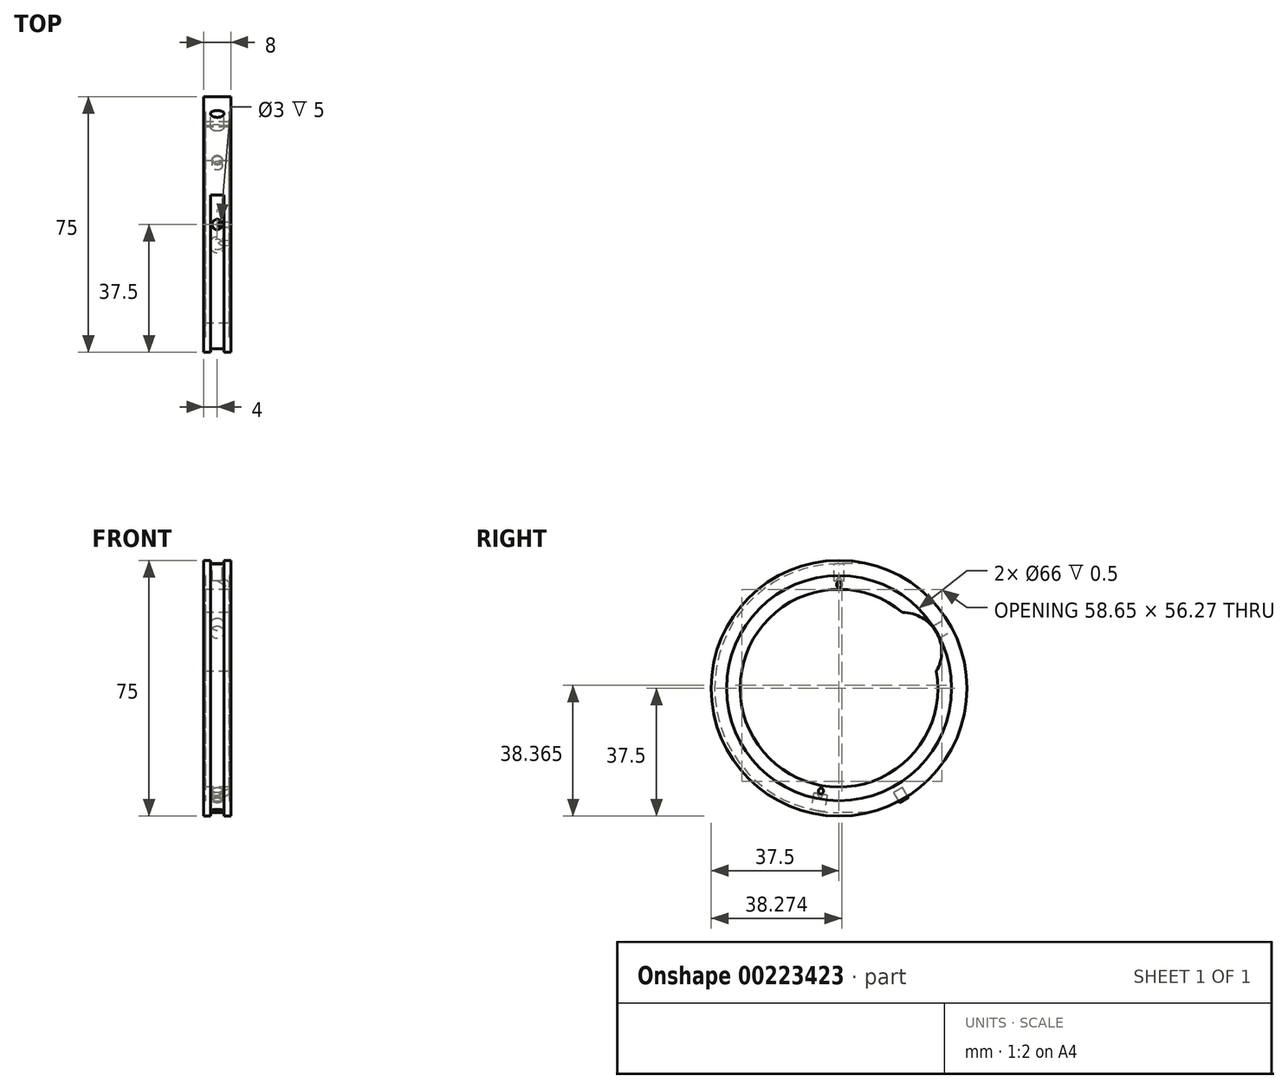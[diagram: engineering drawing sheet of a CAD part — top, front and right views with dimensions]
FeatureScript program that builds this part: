
annotation { "Feature Type Name" : "Feature", "Feature Type Description" : "" }
export const myFeature = defineFeature(function(context is Context, id is Id, definition is map)
    precondition{}
    {
        {
            var Q0;
            Q0=qCreatedBy(makeId("Front.planeOp"),FACE);
            var sketch = newSketch(context, id + "F0", { "sketchPlane" : qUnion([Q0])});
            skLineSegment(sketch, "E0", {"start": v(-4, 37.5) * mm, "end": v(4, 37.5) * mm});
            skLineSegment(sketch, "E1", {"start": v(4, 37.5) * mm, "end": v(4, 33) * mm});
            skLineSegment(sketch, "E2", {"start": v(4, 33) * mm, "end": v(3.5, 33) * mm});
            skLineSegment(sketch, "E3", {"start": v(3.5, 33) * mm, "end": v(3.5, 29) * mm});
            skLineSegment(sketch, "E4", {"start": v(3.5, 29) * mm, "end": v(0, 29) * mm});
            skLineSegment(sketch, "E5.MirrorCS", {"start": v(-4, 33) * mm, "end": v(-3.5, 33) * mm});
            skLineSegment(sketch, "E6.MirrorCS", {"start": v(-3.5, 29) * mm, "end": v(0, 29) * mm});
            skLineSegment(sketch, "E7.MirrorCS", {"start": v(-3.5, 33) * mm, "end": v(-3.5, 29) * mm});
            skLineSegment(sketch, "E8.MirrorCS", {"start": v(-4, 37.5) * mm, "end": v(-4, 33) * mm});
            skLineSegment(sketch, "E9", {"start": v(-6.02, 0) * mm, "end": v(8.87, 0) * mm});
            skSolve(sketch);
        }
        {
            var Q0;
            Q0=makeQuery(id+"F0.imprint","IMPRINT",FACE,{"disambiguationData":[TD([[makeQuery(id+"F0.imprint","IMPRINT",EDGE,{"derivedFrom":sQuery(id+"F0.wireOp",EDGE,"E0")}),-1.0]])]});
            var Q1;
            Q1=sQuery(id+"F0.wireOp",EDGE,"E9");
            revolve(context, id + "F1", {"entities" : qUnion([Q0]), "axis" : qUnion([Q1]), "revolveType" : RevolveType.FULL});
        }
        {
            var Q0;
            Q0=qCreatedBy(makeId("Front.planeOp"),FACE);
            var sketch = newSketch(context, id + "F2", { "sketchPlane" : qUnion([Q0])});
            skLineSegment(sketch, "E10.bottom", {"start": v(-2, 38.5) * mm, "end": v(2, 38.5) * mm});
            skLineSegment(sketch, "E10.top", {"start": v(-2, 36.5) * mm, "end": v(2, 36.5) * mm});
            skLineSegment(sketch, "E10.left", {"start": v(-2, 38.5) * mm, "end": v(-2, 36.5) * mm});
            skLineSegment(sketch, "E10.right", {"start": v(2, 38.5) * mm, "end": v(2, 36.5) * mm});
            skPoint(sketch, "E10.middle", {"position": v(0, 37.5) * mm});
            skLineSegment(sketch, "E11", {"start": v(0, 0) * mm, "end": v(5.52, 0) * mm});
            skPoint(sketch, "E12.orphan", {"position": v(4, 37.5) * mm});
            skPoint(sketch, "E13.orphan", {"position": v(-4, 37.5) * mm});
            skSolve(sketch);
        }
        {
            var Q0;
            {var subQ5=sQuery(id+"F2.wireOp",EDGE,"E10.bottom");Q0=makeQuery(id+"F2.imprint","IMPRINT",FACE,{"disambiguationData":[TD([[makeQuery(id+"F2.imprint","IMPRINT",EDGE,{"derivedFrom":subQ5}),-1.0]])]});}
            var Q1;
            {var subQ5=sQuery(id+"F2.wireOp",EDGE,"E10.top");Q1=makeQuery(id+"F2.imprint","IMPRINT",FACE,{"disambiguationData":[TD([[makeQuery(id+"F2.imprint","IMPRINT",EDGE,{"derivedFrom":subQ5}),1.0]])]});}
            extrude(context, id + "F3", {"entities" : qUnion([Q0, Q1]), "operationType" : NewBodyOperationType.REMOVE, "endBound" : BoundingType.SYMMETRIC, "oppositeDirection" : true, "depth" : 25 * mm});
        }
        {
            var Q0;
            Q0=makeQuery(id+"F3.boolean.opBoolean","COPY",FACE,{"derivedFrom":makeQuery(id+"F3.opExtrude","SWEPT_FACE",FACE,{"disambiguationData":[OSD([sQuery(id+"F2.wireOp",EDGE,"E10.top")])]})});
            var sketch = newSketch(context, id + "F4", { "sketchPlane" : qUnion([Q0])});
            skPoint(sketch, "E14", {"position": v(0, 0) * mm});
            skCircle(sketch, "E15", {"center": v(0, 0) * mm, "radius": 1.5 * mm});
            skSolve(sketch);
        }
        {
            var Q0;
            Q0=makeQuery(id+"F4.imprint","IMPRINT",FACE,{"disambiguationData":[TD([[makeQuery(id+"F4.imprint","IMPRINT",EDGE,{"derivedFrom":sQuery(id+"F4.wireOp",EDGE,"E15")}),1.0]])]});
            extrude(context, id + "F5", {"entities" : qUnion([Q0]), "operationType" : NewBodyOperationType.REMOVE, "oppositeDirection" : true, "depth" : 5 * mm});
        }
        {
            var Q0;
            Q0=makeQuery(id+"F1.opRevolve","SWEPT_FACE",FACE,{"disambiguationData":[OSD([sQuery(id+"F0.wireOp",EDGE,"E7.MirrorCS")])]});
            var sketch = newSketch(context, id + "F6", { "sketchPlane" : qUnion([Q0])});
            skArc(sketch, "E16", {"start": v(-18.66, 22.2) * mm, "mid": v(-28.57, 16.43) * mm, "end": v(-28.57, 4.97) * mm});
            skArc(sketch, "E17.0", {"start": v(-18.66, 22.2) * mm, "mid": v(-25.14, 14.46) * mm, "end": v(-28.57, 4.97) * mm});
            skSolve(sketch);
        }
        {
            var Q0;
            Q0=makeQuery(id+"F6.imprint","IMPRINT",FACE,{"disambiguationData":[TD([[makeQuery(id+"F6.imprint","IMPRINT",EDGE,{"derivedFrom":sQuery(id+"F6.wireOp",EDGE,"E16")}),1.0]])]});
            extrude(context, id + "F7", {"entities" : qUnion([Q0]), "operationType" : NewBodyOperationType.REMOVE, "oppositeDirection" : true, "depth" : 7.5 * mm});
        }
        {
            var Q0;
            Q0=qCreatedBy(makeId("Right.planeOp"),FACE);
            var sketch = newSketch(context, id + "F8", { "sketchPlane" : qUnion([Q0])});
            skLineSegment(sketch, "E18", {"start": v(32.48, 18.75) * mm, "end": v(0, 0) * mm});
            skCircle(sketch, "E19.0", {"center": v(0, 0) * mm, "radius": 37.5 * mm});
            skPoint(sketch, "E20", {"position": v(32.48, 18.75) * mm});
            skSolve(sketch);
        }
        {
            var Q0;
            Q0=sQuery(id+"F8.wireOp",EDGE,"E18");
            var Q1;
            Q1=sQuery(id+"F8.wireOp",VERTEX,"E20");
            cPlane(context, id + "F9", {"entities" : qUnion([Q0, Q1]), "cplaneType" : CPlaneType.CURVE_POINT, "offset" : 25 * mm, "width" : 150 * mm, "height" : 150 * mm});
        }
        {
            var Q0;
            Q0=qCreatedBy(id+"F9.planeOp",FACE);
            var sketch = newSketch(context, id + "F10", { "sketchPlane" : qUnion([Q0])});
            skCircle(sketch, "E21", {"center": v(0, 0) * mm, "radius": 2 * mm});
            skSolve(sketch);
        }
        {
            var Q0;
            Q0=makeQuery(id+"F10.imprint","IMPRINT",FACE,{"disambiguationData":[TD([[makeQuery(id+"F10.imprint","IMPRINT",EDGE,{"derivedFrom":sQuery(id+"F10.wireOp",EDGE,"E21")}),1.0]])]});
            extrude(context, id + "F11", {"entities" : qUnion([Q0]), "operationType" : NewBodyOperationType.REMOVE, "depth" : 25 * mm});
        }
        {
            var Q0;
            Q0=qCreatedBy(makeId("Right.planeOp"),FACE);
            var sketch = newSketch(context, id + "F12", { "sketchPlane" : qUnion([Q0])});
            skLineSegment(sketch, "E22", {"start": v(0, 0) * mm, "end": v(18.75, -32.48) * mm});
            skCircle(sketch, "E23.0", {"center": v(0, 0) * mm, "radius": 37.5 * mm});
            skPoint(sketch, "E24", {"position": v(18.75, -32.48) * mm});
            skLineSegment(sketch, "E25.0", {"start": v(32.48, 18.75) * mm, "end": v(0, 0) * mm});
            skSolve(sketch);
        }
        {
            var Q0;
            Q0=sQuery(id+"F12.wireOp",EDGE,"E22");
            var Q1;
            Q1=sQuery(id+"F12.wireOp",VERTEX,"E24");
            cPlane(context, id + "F13", {"entities" : qUnion([Q0, Q1]), "cplaneType" : CPlaneType.CURVE_POINT, "offset" : 25 * mm, "width" : 150 * mm, "height" : 150 * mm});
        }
        {
            var Q0;
            Q0=qCreatedBy(id+"F13.planeOp",FACE);
            var sketch = newSketch(context, id + "F14", { "sketchPlane" : qUnion([Q0])});
            skCircle(sketch, "E26", {"center": v(0, 0) * mm, "radius": 1.5 * mm});
            skSolve(sketch);
        }
        {
            var Q0;
            Q0=makeQuery(id+"F14.imprint","IMPRINT",FACE,{"disambiguationData":[TD([[makeQuery(id+"F14.imprint","IMPRINT",EDGE,{"derivedFrom":sQuery(id+"F14.wireOp",EDGE,"E26")}),1.0]])]});
            extrude(context, id + "F15", {"entities" : qUnion([Q0]), "operationType" : NewBodyOperationType.REMOVE, "oppositeDirection" : true, "depth" : 3 * mm});
        }
        {
            var Q0;
            Q0=qCreatedBy(makeId("Front.planeOp"),FACE);
            var sketch = newSketch(context, id + "F16", { "sketchPlane" : qUnion([Q0])});
            skLineSegment(sketch, "E27", {"start": v(-4, 37.5) * mm, "end": v(4, 37.5) * mm});
            skLineSegment(sketch, "E28", {"start": v(4, -37.5) * mm, "end": v(-4, -37.5) * mm});
            skLineSegment(sketch, "E29.0", {"start": v(4, 30.06) * mm, "end": v(4, 37.5) * mm, "construction": true});
            skLineSegment(sketch, "E30", {"start": v(1.5, 31.5) * mm, "end": v(4, 30.06) * mm});
            skPoint(sketch, "E31.orphan", {"position": v(4, -37.5) * mm});
            skPoint(sketch, "E32.0.start.orphan", {"position": v(-1.5, 31.5) * mm});
            skPoint(sketch, "E33", {"position": v(4, 30.06) * mm});
            skSolve(sketch);
        }
        {
            var Q0;
            Q0=sQuery(id+"F16.wireOp",EDGE,"E30");
            var Q1;
            Q1=sQuery(id+"F16.wireOp",VERTEX,"E33");
            cPlane(context, id + "F17", {"entities" : qUnion([Q0, Q1]), "cplaneType" : CPlaneType.CURVE_POINT, "offset" : 25 * mm, "width" : 150 * mm, "height" : 150 * mm});
        }
        {
            var Q0;
            Q0=qCreatedBy(id+"F17.planeOp",FACE);
            var sketch = newSketch(context, id + "F18", { "sketchPlane" : qUnion([Q0])});
            skPoint(sketch, "E34.0", {"position": v(0, 28.03) * mm});
            skCircle(sketch, "E35", {"center": v(0, 28.03) * mm, "radius": 0.75 * mm});
            skSolve(sketch);
        }
        {
            var Q0;
            Q0=makeQuery(id+"F18.imprint","IMPRINT",FACE,{"disambiguationData":[TD([[makeQuery(id+"F18.imprint","IMPRINT",EDGE,{"derivedFrom":sQuery(id+"F18.wireOp",EDGE,"E35")}),1.0]])]});
            var Q1;
            Q1=sQuery(id+"F16.wireOp",VERTEX,"E32.0.start.orphan");
            extrude(context, id + "F19", {"entities" : qUnion([Q0]), "operationType" : NewBodyOperationType.REMOVE, "endBound" : BoundingType.UP_TO_VERTEX, "oppositeDirection" : true, "endBoundEntityVertex" : qUnion([Q1]), "depth" : 4 * mm});
        }
        {
            var Q0;
            Q0=qCreatedBy(makeId("Right.planeOp"),FACE);
            var sketch = newSketch(context, id + "F20", { "sketchPlane" : qUnion([Q0])});
            skLineSegment(sketch, "E36", {"start": v(0, 0) * mm, "end": v(-6.51, -36.93) * mm});
            skCircle(sketch, "E37.0", {"center": v(0, 0) * mm, "radius": 37.5 * mm});
            skPoint(sketch, "E38", {"position": v(-6.51, -36.93) * mm});
            skSolve(sketch);
        }
        {
            var Q0;
            Q0=qCreatedBy(makeId("Front.planeOp"),FACE);
            var Q1;
            Q1=makeQuery(id+"F1.opRevolve","SWEPT_EDGE",EDGE,{"disambiguationData":[OSD([sQuery(id+"F0.wireOp",EDGE,"E3"),sQuery(id+"F0.wireOp",EDGE,"E4")])]});
            cPlane(context, id + "F21", {"entities" : qUnion([Q0, Q1]), "cplaneType" : CPlaneType.LINE_ANGLE, "offset" : 25 * mm, "angle" : 10 * degree, "width" : 150 * mm, "height" : 150 * mm});
        }
        {
            var Q0;
            Q0=sQuery(id+"F20.wireOp",EDGE,"E36");
            var Q1;
            Q1=sQuery(id+"F20.wireOp",VERTEX,"E38");
            cPlane(context, id + "F22", {"entities" : qUnion([Q0, Q1]), "cplaneType" : CPlaneType.CURVE_POINT, "offset" : 25 * mm, "width" : 150 * mm, "height" : 150 * mm});
        }
        {
            var Q0;
            Q0=qCreatedBy(id+"F22.planeOp",FACE);
            var sketch = newSketch(context, id + "F23", { "sketchPlane" : qUnion([Q0])});
            skPoint(sketch, "E39.0", {"position": v(0, 0) * mm});
            skCircle(sketch, "E40", {"center": v(0, 0) * mm, "radius": 2 * mm});
            skSolve(sketch);
        }
        {
            var Q0;
            Q0=makeQuery(id+"F23.imprint","IMPRINT",FACE,{"disambiguationData":[TD([[makeQuery(id+"F23.imprint","IMPRINT",EDGE,{"derivedFrom":sQuery(id+"F23.wireOp",EDGE,"E40")}),1.0]])]});
            var Q1;
            Q1=sQuery(id+"F23.wireOp",EDGE,"E40");
            extrude(context, id + "F24", {"entities" : qUnion([Q0]), "operationType" : NewBodyOperationType.REMOVE, "surfaceEntities" : qUnion([Q1]), "oppositeDirection" : true, "depth" : 6 * mm});
        }
        {
            var Q0;
            Q0=qCreatedBy(id+"F21.planeOp",FACE);
            var sketch = newSketch(context, id + "F25", { "sketchPlane" : qUnion([Q0])});
            skLineSegment(sketch, "E41", {"start": v(4, -37.5) * mm, "end": v(-4, -37.5) * mm});
            skLineSegment(sketch, "E42.0", {"start": v(-3.5, 29) * mm, "end": v(-3.5, -29) * mm});
            skLineSegment(sketch, "E43.0", {"start": v(3.5, 29) * mm, "end": v(3.5, -29) * mm});
            skLineSegment(sketch, "E44.0", {"start": v(-3.5, 33) * mm, "end": v(-3.5, -33) * mm});
            skLineSegment(sketch, "E45.0", {"start": v(4, 33) * mm, "end": v(4, -33) * mm});
            skLineSegment(sketch, "E46.0", {"start": v(2, -31.5) * mm, "end": v(-2, -31.5) * mm});
            skLineSegment(sketch, "E47", {"start": v(-2, -31.5) * mm, "end": v(-3.5, -30.63) * mm});
            skSolve(sketch);
        }
        {
            var Q0;
            Q0=sQuery(id+"F25.wireOp",EDGE,"E47");
            var Q1;
            Q1=sQuery(id+"F25.wireOp",VERTEX,"E47.end");
            cPlane(context, id + "F26", {"entities" : qUnion([Q0, Q1]), "cplaneType" : CPlaneType.CURVE_POINT, "offset" : 25 * mm, "width" : 150 * mm, "height" : 150 * mm});
        }
        {
            var Q0;
            Q0=qCreatedBy(id+"F26.planeOp",FACE);
            var sketch = newSketch(context, id + "F27", { "sketchPlane" : qUnion([Q0])});
            skPoint(sketch, "E48.0", {"position": v(-4.27, -27.96) * mm});
            skCircle(sketch, "E49", {"center": v(-4.27, -27.96) * mm, "radius": 0.75 * mm});
            skSolve(sketch);
        }
        {
            var Q0;
            Q0=makeQuery(id+"F27.imprint","IMPRINT",FACE,{"disambiguationData":[TD([[makeQuery(id+"F27.imprint","IMPRINT",EDGE,{"derivedFrom":sQuery(id+"F27.wireOp",EDGE,"E49")}),1.0]])]});
            extrude(context, id + "F28", {"entities" : qUnion([Q0]), "operationType" : NewBodyOperationType.REMOVE, "oppositeDirection" : true, "depth" : 4.5 * mm});
        }
        {
            var Q0;
            Q0=makeQuery(id+"F28.boolean.opBoolean","COPY",FACE,{"derivedFrom":makeQuery(id+"F28.opExtrude","CAP_FACE",FACE,{"disambiguationData":[OSD([sQuery(id+"F27.wireOp",EDGE,"E49")])],"isStart":true})});
            extrude(context, id + "F29", {"entities" : qUnion([Q0]), "operationType" : NewBodyOperationType.REMOVE, "oppositeDirection" : true, "depth" : 2 * mm});
        }
        {
            var Q0;
            Q0=qCreatedBy(id+"F13.planeOp",FACE);
            var sketch = newSketch(context, id + "F30", { "sketchPlane" : qUnion([Q0])});
            skPoint(sketch, "E50", {"position": v(0, 0) * mm});
            skCircle(sketch, "E51", {"center": v(0, 0) * mm, "radius": 1.48 * mm});
            skSolve(sketch);
        }
        {
            var Q0;
            Q0=makeQuery(id+"F30.imprint","IMPRINT",FACE,{"disambiguationData":[TD([[makeQuery(id+"F30.imprint","IMPRINT",EDGE,{"derivedFrom":sQuery(id+"F30.wireOp",EDGE,"E51")}),1.0]])]});
            extrude(context, id + "F31", {"entities" : qUnion([Q0]), "operationType" : NewBodyOperationType.ADD, "oppositeDirection" : true, "depth" : 3 * mm});
        }
        {
            var Q0;
            Q0=makeQuery(id+"F2.imprint","IMPRINT",FACE,{"disambiguationData":[TD([[makeQuery(id+"F2.imprint","IMPRINT",EDGE,{"derivedFrom":sQuery(id+"F2.wireOp",EDGE,"E10.bottom")}),-1.0]])]});
            var Q1;
            Q1=sQuery(id+"F2.wireOp",EDGE,"E11");
            revolve(context, id + "F32", {"operationType" : NewBodyOperationType.REMOVE, "entities" : qUnion([Q0]), "axis" : qUnion([Q1]), "revolveType" : RevolveType.ONE_DIRECTION, "angle" : 180 * degree});
        }
        {
            var Q0;
            Q0=qCreatedBy(makeId("Front.planeOp"),FACE);
            var sketch = newSketch(context, id + "F33", { "sketchPlane" : qUnion([Q0])});
            skLineSegment(sketch, "E52.bottom", {"start": v(2, -36.5) * mm, "end": v(-2, -36.5) * mm});
            skLineSegment(sketch, "E52.top", {"start": v(2, -38.5) * mm, "end": v(-2, -38.5) * mm});
            skLineSegment(sketch, "E52.left", {"start": v(2, -36.5) * mm, "end": v(2, -38.5) * mm});
            skLineSegment(sketch, "E52.right", {"start": v(-2, -36.5) * mm, "end": v(-2, -38.5) * mm});
            skPoint(sketch, "E52.middle", {"position": v(0, -37.5) * mm});
            skLineSegment(sketch, "E53.0", {"start": v(-2, 37.5) * mm, "end": v(-2, -37.5) * mm});
            skLineSegment(sketch, "E54.0", {"start": v(2, 37.5) * mm, "end": v(2, -37.5) * mm});
            skSolve(sketch);
        }
        {
            var Q0;
            {var subQ2=sQuery(id+"F33.wireOp",EDGE,"E52.bottom");Q0=makeQuery(id+"F33.imprint","IMPRINT",FACE,{"disambiguationData":[TD([[makeQuery(id+"F33.imprint","IMPRINT",EDGE,{"derivedFrom":subQ2}),1.0]])]});}
            extrude(context, id + "F34", {"entities" : qUnion([Q0]), "operationType" : NewBodyOperationType.REMOVE, "endBound" : BoundingType.UP_TO_NEXT, "oppositeDirection" : true, "depth" : 25 * mm});
        }
        {
            var Q0;
            Q0=makeQuery(id+"F31.opExtrude","CAP_FACE",FACE,{"disambiguationData":[OSD([sQuery(id+"F30.wireOp",EDGE,"E51")])],"isStart":true});
            extrude(context, id + "F35", {"entities" : qUnion([Q0]), "operationType" : NewBodyOperationType.ADD, "depth" : 0.5 * mm});
        }
    });
